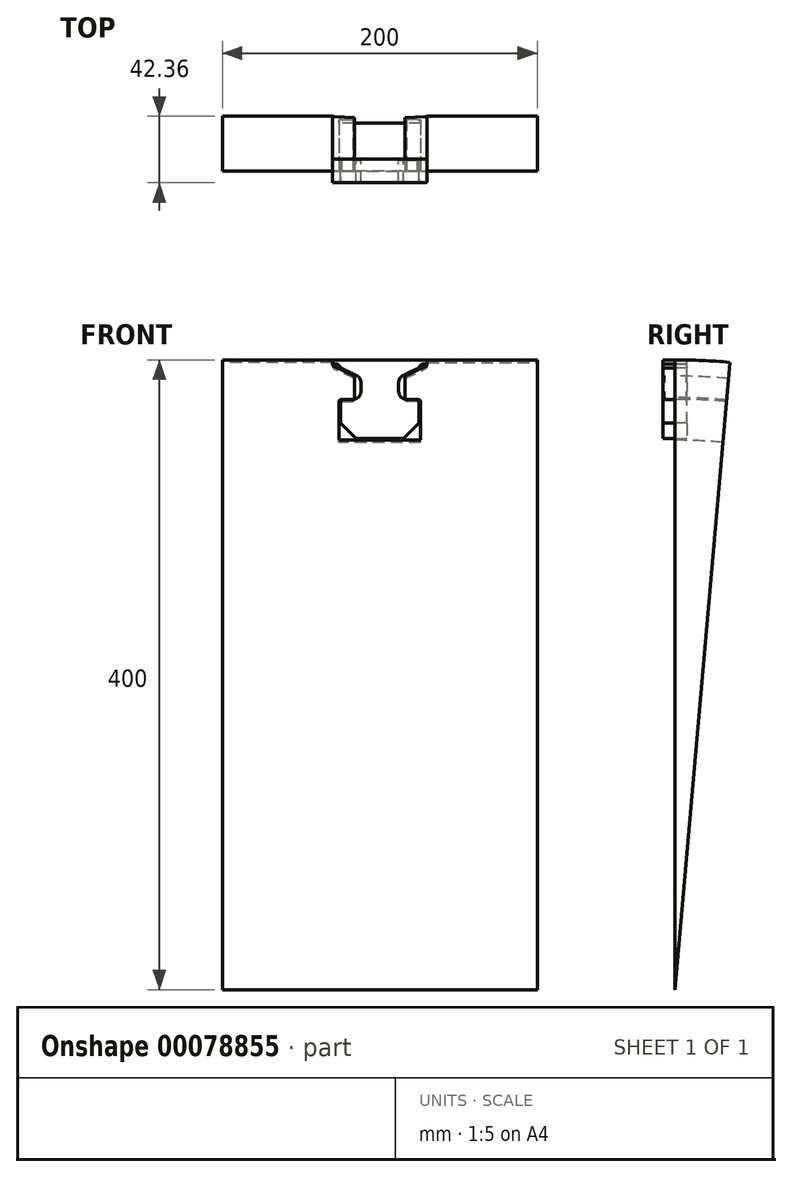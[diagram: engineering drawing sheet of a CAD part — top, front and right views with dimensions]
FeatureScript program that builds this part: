
annotation { "Feature Type Name" : "Feature", "Feature Type Description" : "" }
export const myFeature = defineFeature(function(context is Context, id is Id, definition is map)
    precondition{}
    {
        {
            var Q0;
            Q0=qCreatedBy(makeId("Front.planeOp"),FACE);
            var sketch = newSketch(context, id + "F0", { "sketchPlane" : qUnion([Q0])});
            skLineSegment(sketch, "E0", {"start": v(0, 0) * mm, "end": v(-25, 0) * mm});
            skLineSegment(sketch, "E1", {"start": v(-25, 0) * mm, "end": v(-25, 25) * mm});
            skLineSegment(sketch, "E2", {"start": v(-25, 25) * mm, "end": v(-12, 25) * mm});
            skLineSegment(sketch, "E3", {"start": v(-12, 25) * mm, "end": v(-12, 38.94) * mm});
            skLineSegment(sketch, "E4", {"start": v(-12, 38.94) * mm, "end": v(-25, 45) * mm});
            skLineSegment(sketch, "E5", {"start": v(-30, 50) * mm, "end": v(0, 50) * mm});
            skLineSegment(sketch, "E6", {"start": v(0, 50) * mm, "end": v(0, 0) * mm});
            skLineSegment(sketch, "E7", {"start": v(-25, 47.5) * mm, "end": v(-30, 47.5) * mm});
            skLineSegment(sketch, "E8", {"start": v(-30, 47.5) * mm, "end": v(-30, 50) * mm});
            skLineSegment(sketch, "E9", {"start": v(-25, 45) * mm, "end": v(-25, 47.5) * mm});
            skLineSegment(sketch, "E10", {"start": v(0, -350) * mm, "end": v(-25, -350) * mm, "construction": true});
            skLineSegment(sketch, "E11", {"start": v(-25, 45) * mm, "end": v(-25, 25) * mm});
            skSolve(sketch);
        }
        {
            var Q0;
            Q0=makeQuery(id+"F0.imprint","IMPRINT",FACE,{"disambiguationData":[TD([[makeQuery(id+"F0.imprint","IMPRINT",EDGE,{"derivedFrom":sQuery(id+"F0.wireOp",EDGE,"E0")}),-1.0]])]});
            var Q1;
            Q1=makeQuery(id+"F0.imprint","IMPRINT",FACE,{"disambiguationData":[TD([[makeQuery(id+"F0.imprint","IMPRINT",EDGE,{"derivedFrom":sQuery(id+"F0.wireOp",EDGE,"E2")}),1.0]])]});
            extrude(context, id + "F1", {"entities" : qUnion([Q0, Q1]), "endBound" : BoundingType.SYMMETRIC, "depth" : 15 * mm});
        }
        {
            var Q0;
            Q0=makeQuery(id+"F0.imprint","IMPRINT",FACE,{"disambiguationData":[TD([[makeQuery(id+"F0.imprint","IMPRINT",EDGE,{"derivedFrom":sQuery(id+"F0.wireOp",EDGE,"E2")}),1.0]])]});
            var Q1;
            Q1=sQuery(id+"F0.wireOp",EDGE,"E10");
            revolve(context, id + "F2", {"operationType" : NewBodyOperationType.REMOVE, "entities" : qUnion([Q0]), "axis" : qUnion([Q1]), "revolveType" : RevolveType.FULL, "oppositeDirection" : true});
        }
        {
            var Q0;
            Q0=makeQuery(id+"F2.boolean.opBoolean","COPY",EDGE,{"derivedFrom":makeQuery(id+"F2.opRevolve","SWEPT_EDGE",EDGE,{"disambiguationData":[OSD([sQuery(id+"F0.wireOp",EDGE,"E2"),sQuery(id+"F0.wireOp",EDGE,"E3")])]})});
            fillet(context, id + "F3", {"entities" : qUnion([Q0]), "radius" : 5 * mm, "tangentPropagation" : true, "allowEdgeOverflow" : false});
        }
        {
            var Q0;
            Q0=makeQuery(id+"F2.boolean.opBoolean","COPY",EDGE,{"derivedFrom":makeQuery(id+"F2.opRevolve","SWEPT_EDGE",EDGE,{"disambiguationData":[OSD([sQuery(id+"F0.wireOp",EDGE,"E3"),sQuery(id+"F0.wireOp",EDGE,"E4")])]})});
            fillet(context, id + "F4", {"entities" : qUnion([Q0]), "radius" : 5 * mm, "tangentPropagation" : true, "allowEdgeOverflow" : false});
        }
        {
            var Q0;
            Q0=makeQuery(id+"F1.opExtrude","SWEPT_EDGE",EDGE,{"disambiguationData":[OSD([sQuery(id+"F0.wireOp",EDGE,"E7"),sQuery(id+"F0.wireOp",EDGE,"E9")])]});
            fillet(context, id + "F5", {"entities" : qUnion([Q0]), "radius" : 3 * mm, "tangentPropagation" : true, "allowEdgeOverflow" : false});
        }
        {
            var Q0;
            Q0=makeQuery(id+"F1.opExtrude","SWEPT_EDGE",EDGE,{"disambiguationData":[OSD([sQuery(id+"F0.wireOp",EDGE,"E0"),sQuery(id+"F0.wireOp",EDGE,"E1")])]});
            chamfer(context, id + "F6", {"entities" : qUnion([Q0]), "width" : 10 * mm, "tangentPropagation" : true});
        }
        {
            var Q0;
            Q0=makeQuery(id+"F2.boolean.opBoolean","COPY",EDGE,{"derivedFrom":makeQuery(id+"F2.opRevolve","SWEPT_EDGE",EDGE,{"disambiguationData":[OSD([sQuery(id+"F0.wireOp",EDGE,"E1"),sQuery(id+"F0.wireOp",EDGE,"E2"),sQuery(id+"F0.wireOp",EDGE,"E11")])]})});
            fillet(context, id + "F7", {"entities" : qUnion([Q0]), "radius" : 1 * mm, "tangentPropagation" : true, "allowEdgeOverflow" : false});
        }
        {
            var Q0;
            Q0=makeQuery(id+"F2.boolean.opBoolean","INTERSECT",EDGE,{"derivedFrom":[makeQuery(id+"F1.opExtrude","CAP_FACE",FACE,{"disambiguationData":[OSD([sQuery(id+"F0.wireOp",EDGE,"E0"),sQuery(id+"F0.wireOp",EDGE,"E1"),sQuery(id+"F0.wireOp",EDGE,"E5"),sQuery(id+"F0.wireOp",EDGE,"E6"),sQuery(id+"F0.wireOp",EDGE,"E7"),sQuery(id+"F0.wireOp",EDGE,"E8"),sQuery(id+"F0.wireOp",EDGE,"E9"),sQuery(id+"F0.wireOp",EDGE,"E11")])],"isStart":false}),makeQuery(id+"F2.opRevolve","SWEPT_FACE",FACE,{"disambiguationData":[OSD([sQuery(id+"F0.wireOp",EDGE,"E2")])]})]});
            var Q1;
            Q1=makeQuery(id+"F2.boolean.opBoolean","INTERSECT",EDGE,{"derivedFrom":[makeQuery(id+"F1.opExtrude","CAP_FACE",FACE,{"disambiguationData":[OSD([sQuery(id+"F0.wireOp",EDGE,"E0"),sQuery(id+"F0.wireOp",EDGE,"E1"),sQuery(id+"F0.wireOp",EDGE,"E5"),sQuery(id+"F0.wireOp",EDGE,"E6"),sQuery(id+"F0.wireOp",EDGE,"E7"),sQuery(id+"F0.wireOp",EDGE,"E8"),sQuery(id+"F0.wireOp",EDGE,"E9"),sQuery(id+"F0.wireOp",EDGE,"E11")])],"isStart":true}),makeQuery(id+"F2.opRevolve","SWEPT_FACE",FACE,{"disambiguationData":[OSD([sQuery(id+"F0.wireOp",EDGE,"E2")])]})]});
            fillet(context, id + "F8", {"entities" : qUnion([Q0, Q1]), "radius" : 0.5 * mm, "tangentPropagation" : true, "allowEdgeOverflow" : false});
        }
        {
            var Q0;
            Q0=makeQuery(id+"F1.opExtrude","SWEPT_BODY",BODY,{"disambiguationData":[OSD([sQuery(id+"F0.wireOp",EDGE,"E0"),sQuery(id+"F0.wireOp",EDGE,"E1"),sQuery(id+"F0.wireOp",EDGE,"E5"),sQuery(id+"F0.wireOp",EDGE,"E6"),sQuery(id+"F0.wireOp",EDGE,"E7"),sQuery(id+"F0.wireOp",EDGE,"E8"),sQuery(id+"F0.wireOp",EDGE,"E9"),sQuery(id+"F0.wireOp",EDGE,"E11")])]});
            var Q1;
            Q1=qCreatedBy(makeId("Right.planeOp"),FACE);
            mirror(context, id + "F9", {"operationType" : NewBodyOperationType.ADD, "entities" : qUnion([Q0]), "mirrorPlane" : qUnion([Q1])});
        }
        {
            var Q0;
            Q0=qCreatedBy(makeId("Front.planeOp"),FACE);
            var sketch = newSketch(context, id + "F10", { "sketchPlane" : qUnion([Q0])});
            skLineSegment(sketch, "E12", {"start": v(-26, 25) * mm, "end": v(-16, 25) * mm});
            skLineSegment(sketch, "E13", {"start": v(-16, 25) * mm, "end": v(-16, 39.7) * mm});
            skLineSegment(sketch, "E14", {"start": v(-16, 39.7) * mm, "end": v(-30, 46.23) * mm});
            skLineSegment(sketch, "E15", {"start": v(-30, 46.23) * mm, "end": v(-30, 50) * mm});
            skLineSegment(sketch, "E16", {"start": v(-30, 50) * mm, "end": v(-100, 50) * mm});
            skLineSegment(sketch, "E17", {"start": v(-100, 50) * mm, "end": v(-100, -350) * mm});
            skLineSegment(sketch, "E18", {"start": v(-100, -350) * mm, "end": v(0, -350) * mm});
            skLineSegment(sketch, "E19", {"start": v(0, -350) * mm, "end": v(0, -1) * mm});
            skLineSegment(sketch, "E20", {"start": v(0, -1) * mm, "end": v(-26, -1) * mm});
            skLineSegment(sketch, "E21", {"start": v(-26, -1) * mm, "end": v(-26, 25) * mm});
            skSolve(sketch);
        }
        {
            var Q0;
            Q0=qSketchRegion(id+"F10",true);
            var Q1;
            Q1=sQuery(id+"F10.wireOp",EDGE,"E18");
            revolve(context, id + "F11", {"entities" : qUnion([Q0]), "axis" : qUnion([Q1]), "revolveType" : RevolveType.ONE_DIRECTION, "oppositeDirection" : true, "angle" : 5 * degree});
        }
        {
            var Q0;
            Q0=makeQuery(id+"F11.opRevolve","SWEPT_EDGE",EDGE,{"disambiguationData":[OSD([sQuery(id+"F10.wireOp",EDGE,"E12"),sQuery(id+"F10.wireOp",EDGE,"E13")])]});
            chamfer(context, id + "F12", {"entities" : qUnion([Q0]), "width" : 1 * mm, "tangentPropagation" : true});
        }
        {
            var Q0;
            Q0=makeQuery(id+"F11.opRevolve","SWEPT_EDGE",EDGE,{"disambiguationData":[OSD([sQuery(id+"F10.wireOp",EDGE,"E14"),sQuery(id+"F10.wireOp",EDGE,"E15")])]});
            fillet(context, id + "F13", {"entities" : qUnion([Q0]), "radius" : 2 * mm, "tangentPropagation" : true, "allowEdgeOverflow" : false});
        }
        {
            var Q0;
            Q0=makeQuery(id+"F11.opRevolve","SWEPT_EDGE",EDGE,{"disambiguationData":[OSD([sQuery(id+"F10.wireOp",EDGE,"E12"),sQuery(id+"F10.wireOp",EDGE,"E21")])]});
            fillet(context, id + "F14", {"entities" : qUnion([Q0]), "radius" : 2 * mm, "tangentPropagation" : true, "allowEdgeOverflow" : false});
        }
        {
            var Q0;
            Q0=makeQuery(id+"F11.opRevolve","SWEPT_BODY",BODY,{"disambiguationData":[OSD([sQuery(id+"F10.wireOp",EDGE,"E12"),sQuery(id+"F10.wireOp",EDGE,"E13"),sQuery(id+"F10.wireOp",EDGE,"E14"),sQuery(id+"F10.wireOp",EDGE,"E15"),sQuery(id+"F10.wireOp",EDGE,"E16"),sQuery(id+"F10.wireOp",EDGE,"E17"),sQuery(id+"F10.wireOp",EDGE,"E18"),sQuery(id+"F10.wireOp",EDGE,"E19"),sQuery(id+"F10.wireOp",EDGE,"E20"),sQuery(id+"F10.wireOp",EDGE,"E21")])]});
            var Q1;
            Q1=qCreatedBy(makeId("Right.planeOp"),FACE);
            mirror(context, id + "F15", {"operationType" : NewBodyOperationType.ADD, "entities" : qUnion([Q0]), "mirrorPlane" : qUnion([Q1])});
        }
    });
